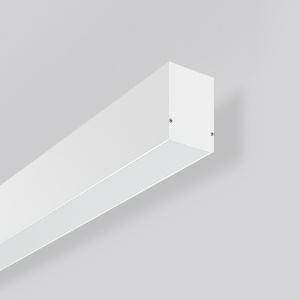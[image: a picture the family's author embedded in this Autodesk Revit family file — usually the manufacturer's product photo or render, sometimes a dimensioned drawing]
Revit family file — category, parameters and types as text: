
# Revit family: less_is_more_50_312614_002_1_6fc2
name_source: partatom
category: Lighting Fixtures
units: mm (PartAtom-declared; Revit-internal decimal feet)

## family parameters
Cut with Voids When Loaded = No
Host = Face
Light Source = No
Part Type = Normal
Room Calculation Point = No
Round Connector Dimension = Use Diameter
Shared = No

## types (1)
- LESS IS MORE 50 (1 x LED Modul 840, 4800 lm, 4000)
    Apparent Load = 34 VA
    CIE Flux Codes = 48 80 96 50 100
    Color Rendering = 80
    Color Temperature = 4000
    Default Elevation = 1800 mm
    Description = Series: LESS IS MORE 50
Linear wall luminaires. Housing: extruded aluminium profile, powder-coated. End cap aluminium powder-coated. Diffuser made of non-yellowing plastic (PMMA), opal. Direct 50%, indirect 50% light emission. Suitable for Wall (surface). LED unit with integrated converter interchangeable and removable. Suitable for through-wiring. With sensors or as a safety luminaire on request. 
Colour: traffic white, matt (RAL 9016)
Length: 1967 mm
Width: 67 mm
Height: 75 mm
Lamp: LED
Socket: without socket
Colour temperature: 4000K
Colour rendering index (CRI): 80
Light source: LED
Socket lamp2: Without base
Colour temperature: 4000K
Colour rendering index (CRI) 2: 80
System power: 34 W
Rated luminous flux: 4800 lm
Luminous efficiency: 141 lm/W
Control gear: Regulated power supply
Control gear: Regulated power supply
Protection class: I
Type of protection: IP 20
    Height = 75 mm
    Lamp = 1 x LED Modul 840
    Lamp Light Flux = 4800 lm
    Lamp count = 1
    Length = 1967 mm
    Lifetime = 50000 h
    Luminous efficacy = 141 lm/W
    Manufacturer = RZB
    ModVariant = No
    Model = 312614.002.1
    Mounting Place = Wall
    Mounting Type = Surface mounted
    Number of Poles = 1
    OnlyDefault = Yes
    Power Factor = 1
    Product Name = LESS IS MORE 50
    Product group = Surface mounted LED linear luminaires
    ProductGroupID = 2007
    Protection Class = Protection class I
    Protection Degree = IP 20
    RLX_Detail_Level = 1
    RLX_Emergency_Light_Flux = 0 lm
    RLX_Emergency_Type = 0
    RLX_Emergency_Type_DB = No
    RlxData = <blob elided: 39569 chars, md5=d74fca3d>
    Socket = socket
    Standby Power = 0 W
    System Light Flux = 4800 lm
    System Power = 34 W
    Type Comments = Product without accessories
    Type Image = 312606.002.jpg
    URL = http://relux.com
    VarID = ---
    Voltage = 0 V
    Weight = 0.00 kg
    Width = 67 mm

## geometry (parser evidence)
native form markers: Blend x4, Sweep x12
no freeform markers — native parametric forms only
